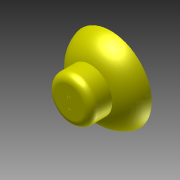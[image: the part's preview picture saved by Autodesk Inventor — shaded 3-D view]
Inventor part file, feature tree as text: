
AUTODESK INVENTOR PART (.ipt)
format: ipt  version: 2012 SP1 (Build 160190100, 190)  size: 166,400 bytes
history: native  units: in
note: dims shown in document units (in); Inventor stores cm internally (conversion verified against a paired STEP export)
features: extrude x4, sketch x4, fillet x2
ambient origin geometry x8: Origin, YZ Plane, XZ Plane, XY Plane, X Axis, Y Axis, Z Axis, Center Point
bodies: Solid1 (feature_tree)
feature tree (10):
  extrude  "Extrusion1"  Depth=0.25in TaperAngle=0.0deg
  fillet  "Fillet1"  Radius=0.3in
  extrude  "Extrusion2"  Depth=0.45in TaperAngle=0.0deg
  fillet  "Fillet2"  Radius=0.075in
  extrude  "Extrusion3"  Depth=0.025in TaperAngle=0.0deg
  extrude  "Extrusion4"  [1 undecoded]
  sketch  "Sketch1"  dims[d0=0.85in d1=0.25in d2=0.0in d3=0.3in]
  sketch  "Sketch2"  dims[d4=0.45in d5=0.45in d6=0.0in d7=0.075in]
  sketch  "Sketch3"  dims[d8=0.0025in d9=0.0in d10=0.025in d11=0.0in]
  sketch  "Sketch4"
note: 1 required parameter value undecoded (feature->parameter linkage not recoverable at this tier; creation-order binding heuristic only, values carry confidence <= 0.55)
